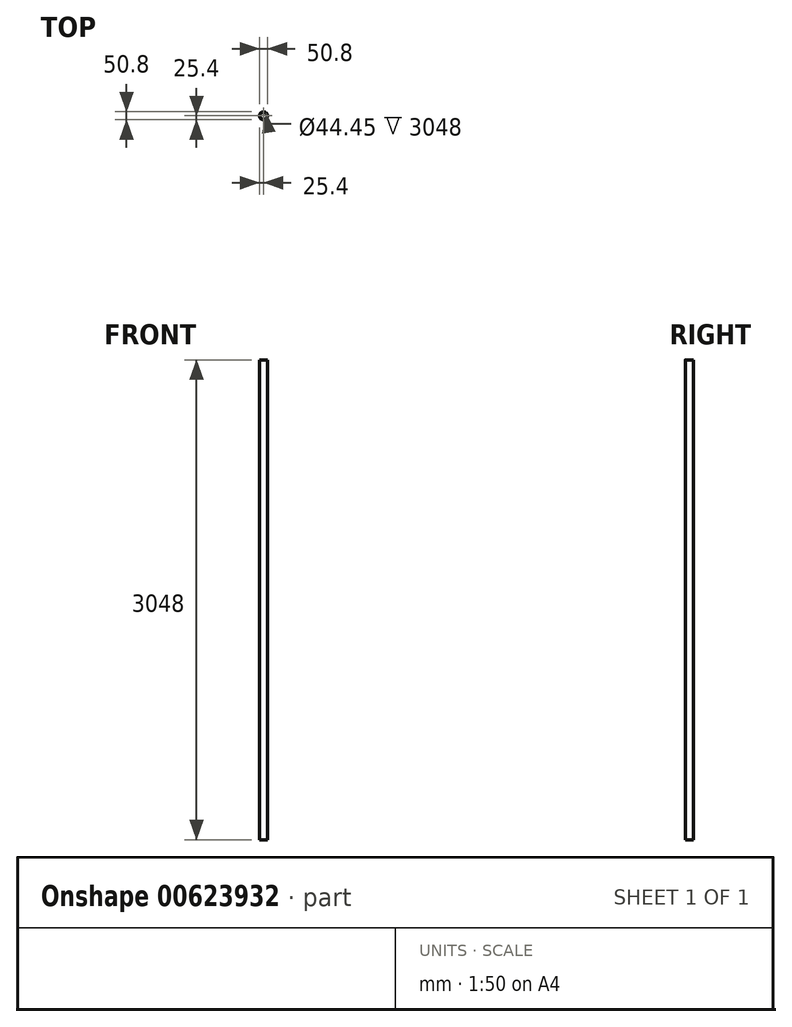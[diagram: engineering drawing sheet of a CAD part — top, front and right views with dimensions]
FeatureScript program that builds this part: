
annotation { "Feature Type Name" : "Feature", "Feature Type Description" : "" }
export const myFeature = defineFeature(function(context is Context, id is Id, definition is map)
    precondition{}
    {
        {
            var Q0;
            Q0=qCreatedBy(makeId("Top.planeOp"),FACE);
            var sketch = newSketch(context, id + "F0", { "sketchPlane" : qUnion([Q0])});
            skCircle(sketch, "E0", {"center": v(0, 0) * mm, "radius": 25.4 * mm});
            skCircle(sketch, "E1", {"center": v(0, 0) * mm, "radius": 22.23 * mm});
            skSolve(sketch);
        }
        {
            var Q0;
            Q0=qSketchRegion(id+"F0",true);
            extrude(context, id + "F1", {"entities" : qUnion([Q0]), "depth" : 3048 * mm, "offsetDistance" : 25.4 * mm});
        }
    });
